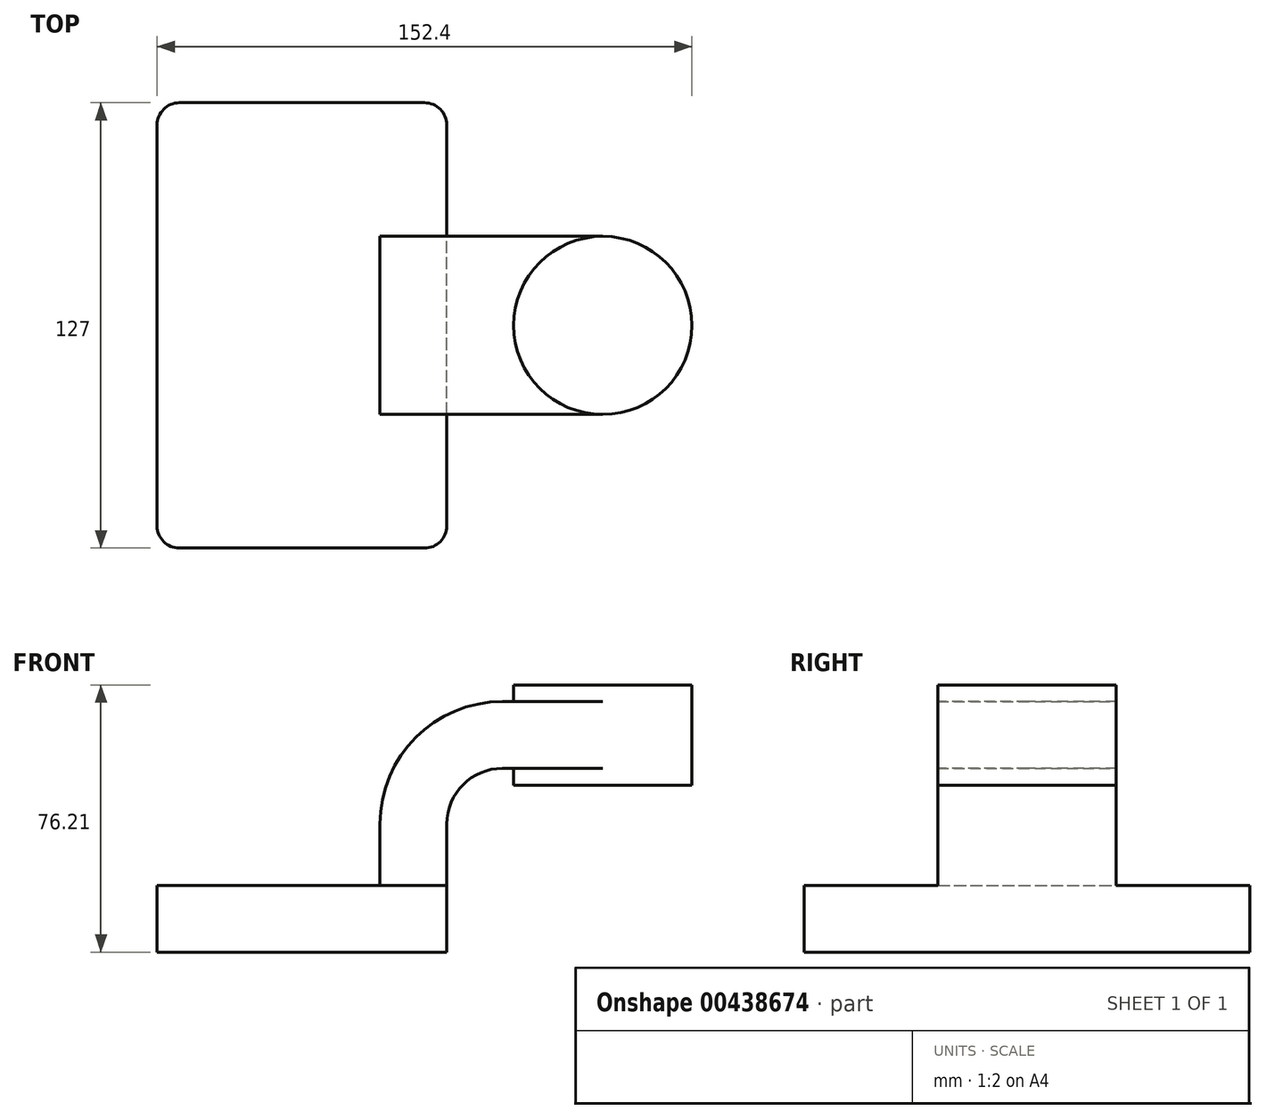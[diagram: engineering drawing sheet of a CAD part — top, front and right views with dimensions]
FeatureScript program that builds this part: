
annotation { "Feature Type Name" : "Feature", "Feature Type Description" : "" }
export const myFeature = defineFeature(function(context is Context, id is Id, definition is map)
    precondition{}
    {
        {
            var Q0;
            Q0=qCreatedBy(makeId("Front.planeOp"),FACE);
            var sketch = newSketch(context, id + "F0", { "sketchPlane" : qUnion([Q0])});
            skLineSegment(sketch, "E0.bottom", {"start": v(-41.28, 9.52) * mm, "end": v(41.28, 9.53) * mm});
            skLineSegment(sketch, "E0.top", {"start": v(-41.27, -9.52) * mm, "end": v(41.28, -9.52) * mm});
            skLineSegment(sketch, "E0.left", {"start": v(-41.28, 9.52) * mm, "end": v(-41.28, -9.53) * mm});
            skLineSegment(sketch, "E0.right", {"start": v(41.27, 9.53) * mm, "end": v(41.28, -9.52) * mm});
            skPoint(sketch, "E0.middle", {"position": v(0, 0) * mm});
            skPoint(sketch, "E1.middle", {"position": v(-41.28, 9.52) * mm});
            skLineSegment(sketch, "E2.bottom", {"start": v(60.32, 38.1) * mm, "end": v(111.12, 38.1) * mm});
            skLineSegment(sketch, "E2.top", {"start": v(60.32, 66.67) * mm, "end": v(111.12, 66.67) * mm});
            skLineSegment(sketch, "E2.left", {"start": v(60.32, 38.1) * mm, "end": v(60.32, 66.67) * mm});
            skLineSegment(sketch, "E2.right", {"start": v(111.12, 38.1) * mm, "end": v(111.12, 66.67) * mm});
            skPoint(sketch, "E2.middle", {"position": v(85.72, 52.39) * mm});
            skLineSegment(sketch, "E3", {"start": v(41.27, 9.53) * mm, "end": v(41.27, 27) * mm});
            skArc(sketch, "E4", {"start": v(41.27, 27) * mm, "mid": v(45.92, 38.23) * mm, "end": v(57.15, 42.88) * mm});
            skLineSegment(sketch, "E5", {"start": v(57.15, 42.88) * mm, "end": v(85.72, 42.88) * mm});
            skLineSegment(sketch, "E6.0", {"start": v(57.15, 61.93) * mm, "end": v(85.72, 61.93) * mm});
            skArc(sketch, "E6.1", {"start": v(22.22, 27) * mm, "mid": v(32.45, 51.7) * mm, "end": v(57.15, 61.93) * mm});
            skLineSegment(sketch, "E6.2", {"start": v(22.22, 9.53) * mm, "end": v(22.22, 27) * mm});
            skLineSegment(sketch, "E7", {"start": v(85.72, 38.1) * mm, "end": v(85.72, 66.67) * mm});
            skFitSpline(sketch, "E8", {"points": [v(-41.27, 9.52) * mm, v(57.15, 61.93) * mm], "startDerivative": vector(-4.04, 86.56) * mm, "endDerivative": vector(133.36, -2.94) * mm});
            skSolve(sketch);
        }
        {
            var Q0;
            Q0=makeQuery(id+"F0.imprint","IMPRINT",FACE,{"disambiguationData":[TD([[makeQuery(id+"F0.imprint","IMPRINT",EDGE,{"derivedFrom":sQuery(id+"F0.wireOp",EDGE,"E0.top")}),1.0]])]});
            extrude(context, id + "F1", {"entities" : qUnion([Q0]), "endBound" : BoundingType.SYMMETRIC, "depth" : 127 * mm});
        }
        {
            var Q0;
            {var subQ0=sQuery(id+"F0.wireOp",EDGE,"E5");var subQ1=sQuery(id+"F0.wireOp",EDGE,"E2.left");var subQ2=makeQuery(id+"F0.imprint","INTERSECT",VERTEX,{"derivedFrom":[subQ1,subQ0]});Q0=makeQuery(id+"F0.imprint","IMPRINT",FACE,{"disambiguationData":[TD([[makeQuery(id+"F0.imprint","IMPRINT",EDGE,{"disambiguationData":[TD([[subQ2,-1.0]])],"derivedFrom":subQ1}),-1.0]])]});}
            var Q1;
            {var subQ1=sQuery(id+"F0.wireOp",EDGE,"E3");Q1=makeQuery(id+"F0.imprint","IMPRINT",FACE,{"disambiguationData":[TD([[makeQuery(id+"F0.imprint","IMPRINT",EDGE,{"derivedFrom":subQ1}),1.0]])]});}
            extrude(context, id + "F2", {"entities" : qUnion([Q0, Q1]), "operationType" : NewBodyOperationType.ADD, "endBound" : BoundingType.SYMMETRIC, "depth" : 50.8 * mm});
        }
        {
            var Q0;
            Q0=makeQuery(id+"F0.imprint","IMPRINT",FACE,{"disambiguationData":[TD([[makeQuery(id+"F0.imprint","IMPRINT",EDGE,{"derivedFrom":sQuery(id+"F0.wireOp",EDGE,"E6.1")}),1.0]])]});
            extrude(context, id + "F3", {"entities" : qUnion([Q0]), "operationType" : NewBodyOperationType.ADD, "endBound" : BoundingType.SYMMETRIC, "depth" : 15.88 * mm});
        }
        {
            var Q0;
            {var subQ0=sQuery(id+"F0.wireOp",EDGE,"E2.right");Q0=makeQuery(id+"F0.imprint","IMPRINT",FACE,{"disambiguationData":[TD([[makeQuery(id+"F0.imprint","IMPRINT",EDGE,{"derivedFrom":subQ0}),1.0]])]});}
            var Q1;
            Q1=sQuery(id+"F0.wireOp",EDGE,"E7");
            revolve(context, id + "F4", {"operationType" : NewBodyOperationType.ADD, "entities" : qUnion([Q0]), "axis" : qUnion([Q1]), "revolveType" : RevolveType.FULL});
        }
        {
            var Q0;
            Q0=makeQuery(id+"F1.opExtrude","CAP_EDGE",EDGE,{"disambiguationData":[OSD([sQuery(id+"F0.wireOp",EDGE,"E0.right")])],"isStart":false});
            var Q1;
            Q1=makeQuery(id+"F1.opExtrude","CAP_EDGE",EDGE,{"disambiguationData":[OSD([sQuery(id+"F0.wireOp",EDGE,"E0.left")])],"isStart":false});
            var Q2;
            Q2=makeQuery(id+"F1.opExtrude","CAP_EDGE",EDGE,{"disambiguationData":[OSD([sQuery(id+"F0.wireOp",EDGE,"E0.right")])],"isStart":true});
            var Q3;
            Q3=makeQuery(id+"F1.opExtrude","CAP_EDGE",EDGE,{"disambiguationData":[OSD([sQuery(id+"F0.wireOp",EDGE,"E0.left")])],"isStart":true});
            fillet(context, id + "F5", {"entities" : qUnion([Q0, Q1, Q2, Q3]), "radius" : 6.35 * mm, "tangentPropagation" : true, "allowEdgeOverflow" : false});
        }
    });
